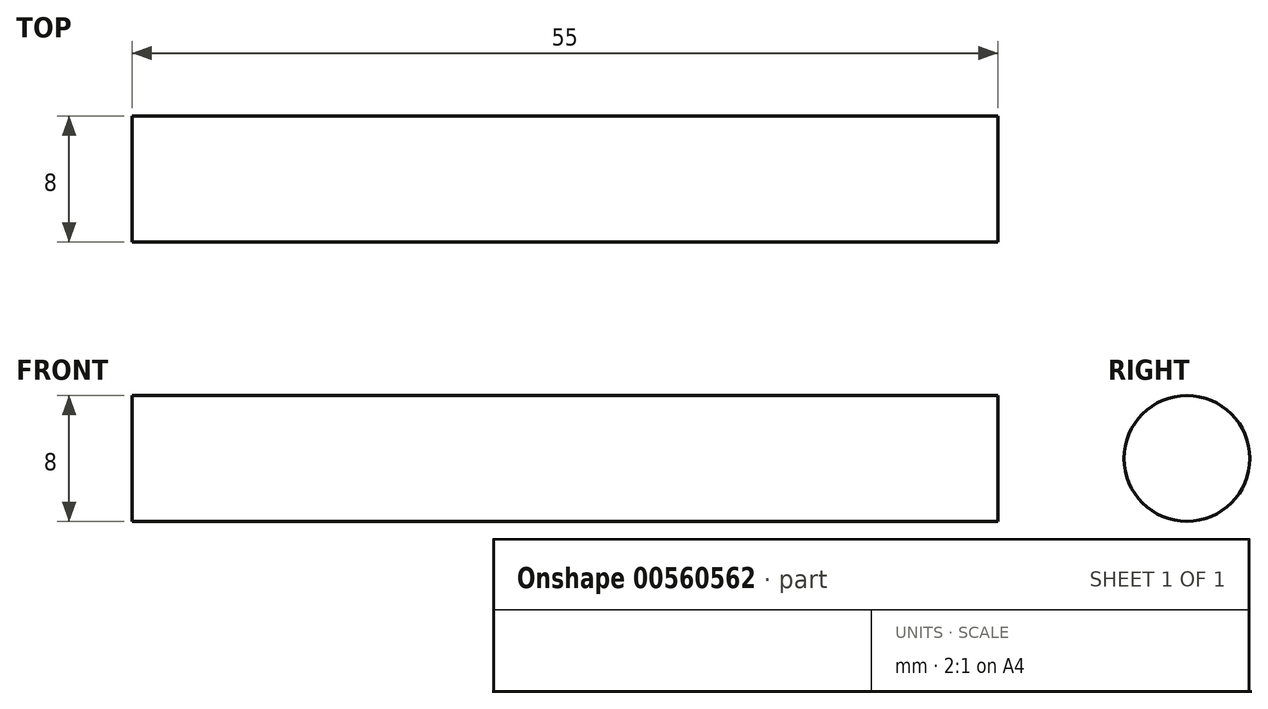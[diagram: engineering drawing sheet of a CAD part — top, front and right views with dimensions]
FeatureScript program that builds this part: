
annotation { "Feature Type Name" : "Feature", "Feature Type Description" : "" }
export const myFeature = defineFeature(function(context is Context, id is Id, definition is map)
    precondition{}
    {
        {
            var Q0;
            Q0=qCreatedBy(makeId("Right.planeOp"),FACE);
            var sketch = newSketch(context, id + "F0", { "sketchPlane" : qUnion([Q0])});
            skCircle(sketch, "E0", {"center": v(0, 0) * mm, "radius": 4 * mm});
            skSolve(sketch);
        }
        {
            var Q0;
            Q0 = qSketchRegion(id + "F0", true);
            extrude(context, id + "F1", {"entities" : qUnion([Q0]), "endBound" : BoundingType.SYMMETRIC, "depth" : 55 * mm, "offsetDistance" : 25 * mm});
        }
    });
